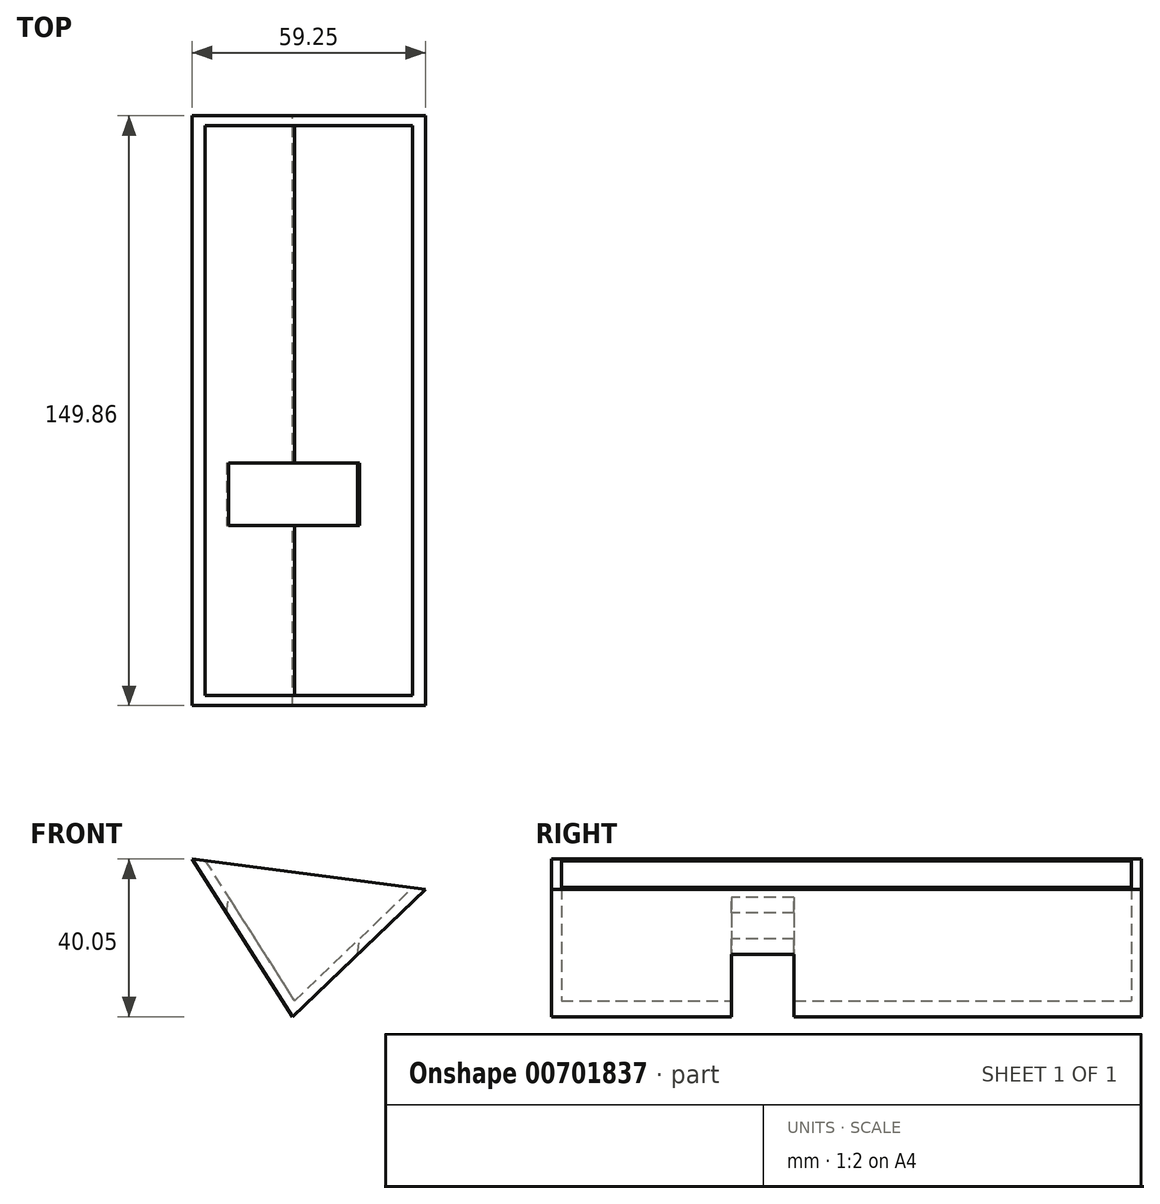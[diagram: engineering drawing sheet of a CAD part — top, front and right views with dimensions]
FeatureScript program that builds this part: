
annotation { "Feature Type Name" : "Feature", "Feature Type Description" : "" }
export const myFeature = defineFeature(function(context is Context, id is Id, definition is map)
    precondition{}
    {
        {
            var Q0;
            Q0=qCreatedBy(makeId("Front.planeOp"),FACE);
            var sketch = newSketch(context, id + "F0", { "sketchPlane" : qUnion([Q0])});
            skLineSegment(sketch, "E0", {"start": v(0, 0) * mm, "end": v(33.74, 32.37) * mm});
            skLineSegment(sketch, "E1", {"start": v(33.74, 32.37) * mm, "end": v(-25.51, 40.05) * mm});
            skLineSegment(sketch, "E2", {"start": v(-25.51, 40.05) * mm, "end": v(0, 0) * mm});
            skSolve(sketch);
        }
        {
            var Q0;
            Q0=makeQuery(id+"F0.imprint","IMPRINT",FACE,{"disambiguationData":[TD([[makeQuery(id+"F0.imprint","IMPRINT",EDGE,{"derivedFrom":sQuery(id+"F0.wireOp",EDGE,"E0")}),1.0]])]});
            extrude(context, id + "F1", {"entities" : qUnion([Q0]), "depth" : 149.86 * mm, "offsetDistance" : 25.4 * mm});
        }
        {
            var Q0;
            Q0=makeQuery(id+"F1.opExtrude","SWEPT_FACE",FACE,{"disambiguationData":[OSD([sQuery(id+"F0.wireOp",EDGE,"E1")])]});
            var sketch = newSketch(context, id + "F2", { "sketchPlane" : qUnion([Q0])});
            skLineSegment(sketch, "E3.bottom", {"start": v(-20.02, -88.2) * mm, "end": v(14.28, -88.2) * mm});
            skLineSegment(sketch, "E3.top", {"start": v(-20.02, -104.14) * mm, "end": v(14.28, -104.14) * mm});
            skLineSegment(sketch, "E3.left", {"start": v(-20.02, -88.2) * mm, "end": v(-20.02, -104.14) * mm});
            skLineSegment(sketch, "E3.right", {"start": v(14.28, -88.2) * mm, "end": v(14.28, -104.14) * mm});
            skSolve(sketch);
        }
        {
            var Q0;
            Q0=makeQuery(id+"F1.opExtrude","SWEPT_FACE",FACE,{"disambiguationData":[OSD([sQuery(id+"F0.wireOp",EDGE,"E1")])]});
            shell(context, id + "F3", {"entities" : qUnion([Q0]), "thickness" : 2.54 * mm});
        }
        {
            var Q0;
            Q0=makeQuery(id+"F2.imprint","IMPRINT",FACE,{"disambiguationData":[TD([[makeQuery(id+"F2.imprint","IMPRINT",EDGE,{"derivedFrom":sQuery(id+"F2.wireOp",EDGE,"E3.bottom")}),-1.0]])]});
            extrude(context, id + "F4", {"entities" : qUnion([Q0]), "operationType" : NewBodyOperationType.REMOVE, "oppositeDirection" : true, "depth" : 94.23 * mm, "offsetDistance" : 25.4 * mm});
        }
    });
